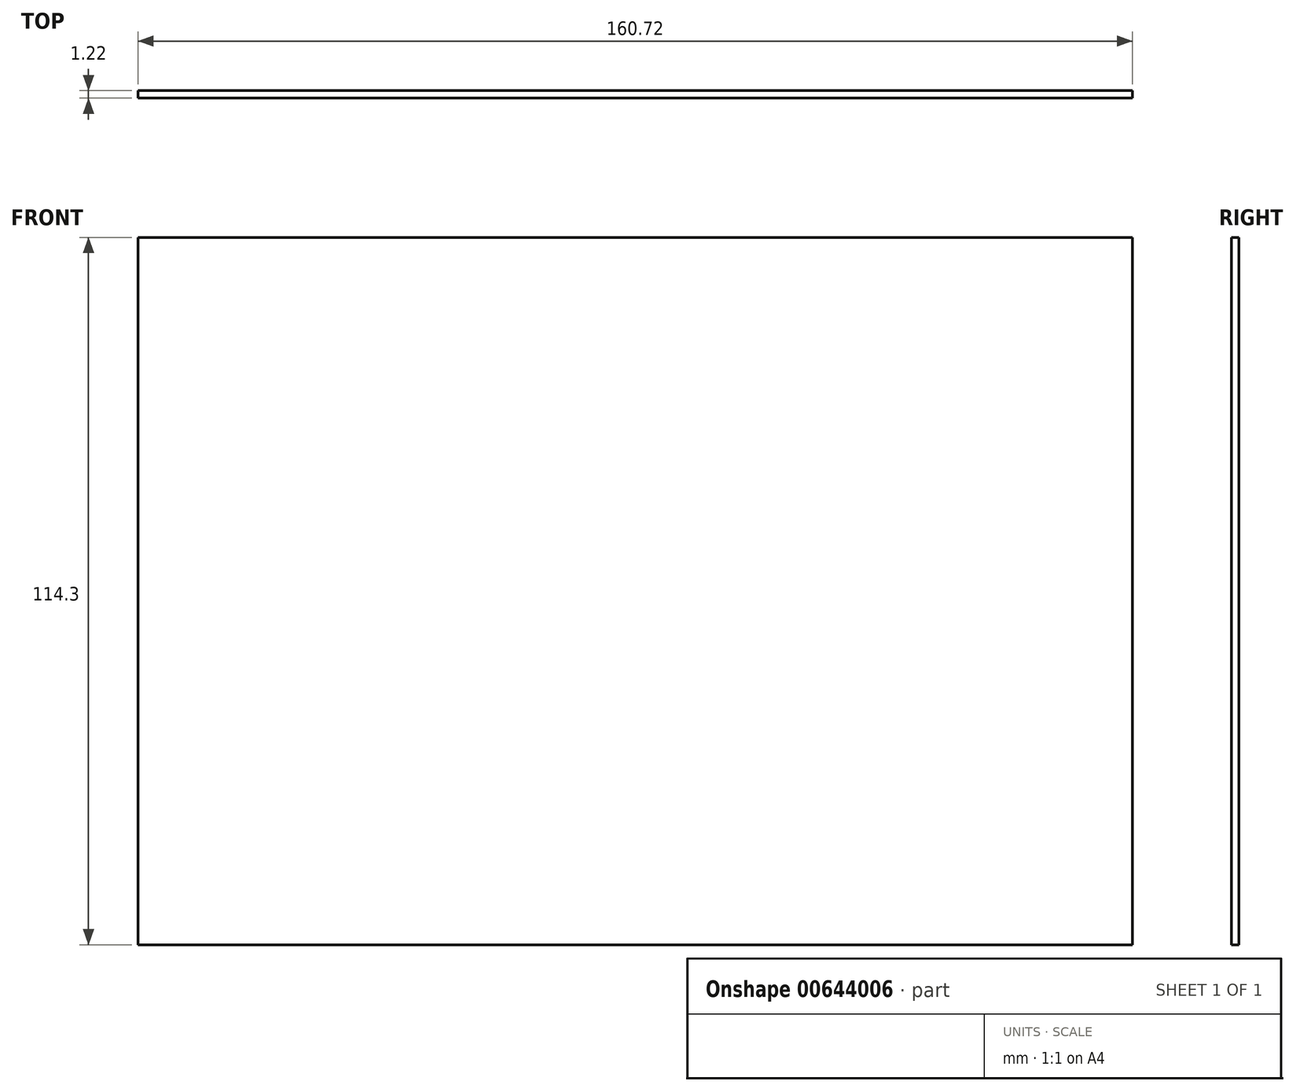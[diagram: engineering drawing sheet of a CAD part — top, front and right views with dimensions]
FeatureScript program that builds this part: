
annotation { "Feature Type Name" : "Feature", "Feature Type Description" : "" }
export const myFeature = defineFeature(function(context is Context, id is Id, definition is map)
    precondition{}
    {
        {
            var Q0;
            Q0=qCreatedBy(makeId("Front.planeOp"),FACE);
            var sketch = newSketch(context, id + "F0", { "sketchPlane" : qUnion([Q0])});
            skLineSegment(sketch, "E0.bottom", {"start": v(0, 0) * mm, "end": v(160.72, 0) * mm});
            skLineSegment(sketch, "E0.top", {"start": v(0, 114.3) * mm, "end": v(160.72, 114.3) * mm});
            skLineSegment(sketch, "E0.left", {"start": v(0, 0) * mm, "end": v(0, 114.3) * mm});
            skLineSegment(sketch, "E0.right", {"start": v(160.72, 0) * mm, "end": v(160.72, 114.3) * mm});
            skSolve(sketch);
        }
        {
            var Q0;
            Q0 = qSketchRegion(id + "F0", true);
            extrude(context, id + "F1", {"entities" : qUnion([Q0]), "depth" : 1.22 * mm, "offsetDistance" : 25.4 * mm});
        }
    });
